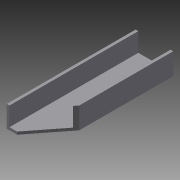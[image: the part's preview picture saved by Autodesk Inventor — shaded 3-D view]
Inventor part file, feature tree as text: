
AUTODESK INVENTOR PART (.ipt)
format: ipt  version: 2014 SP1 (Build 180222100, 222)  size: 87,552 bytes
history: native  units: in
note: dims shown in document units (in); Inventor stores cm internally (conversion verified against a paired STEP export)
features: extrude x2, sketch x2
ambient origin geometry x8: Origin, YZ Plane, XZ Plane, XY Plane, X Axis, Y Axis, Z Axis, Center Point
bodies: Solid1 (feature_tree)
feature tree (4):
  extrude  "Extrusion1"  Depth=1.0in
  extrude  "Extrusion4"  Depth=6.0in TaperAngle=0.0deg
  sketch  "Sketch1"  dims[d0=1.75in d1=1.0in]
  sketch  "Sketch5"  dims[d2=0.125in d3=6.0in d4=0.0in d14=4.375in d15=0.2611in d16=1.0in d17=0.0in]
